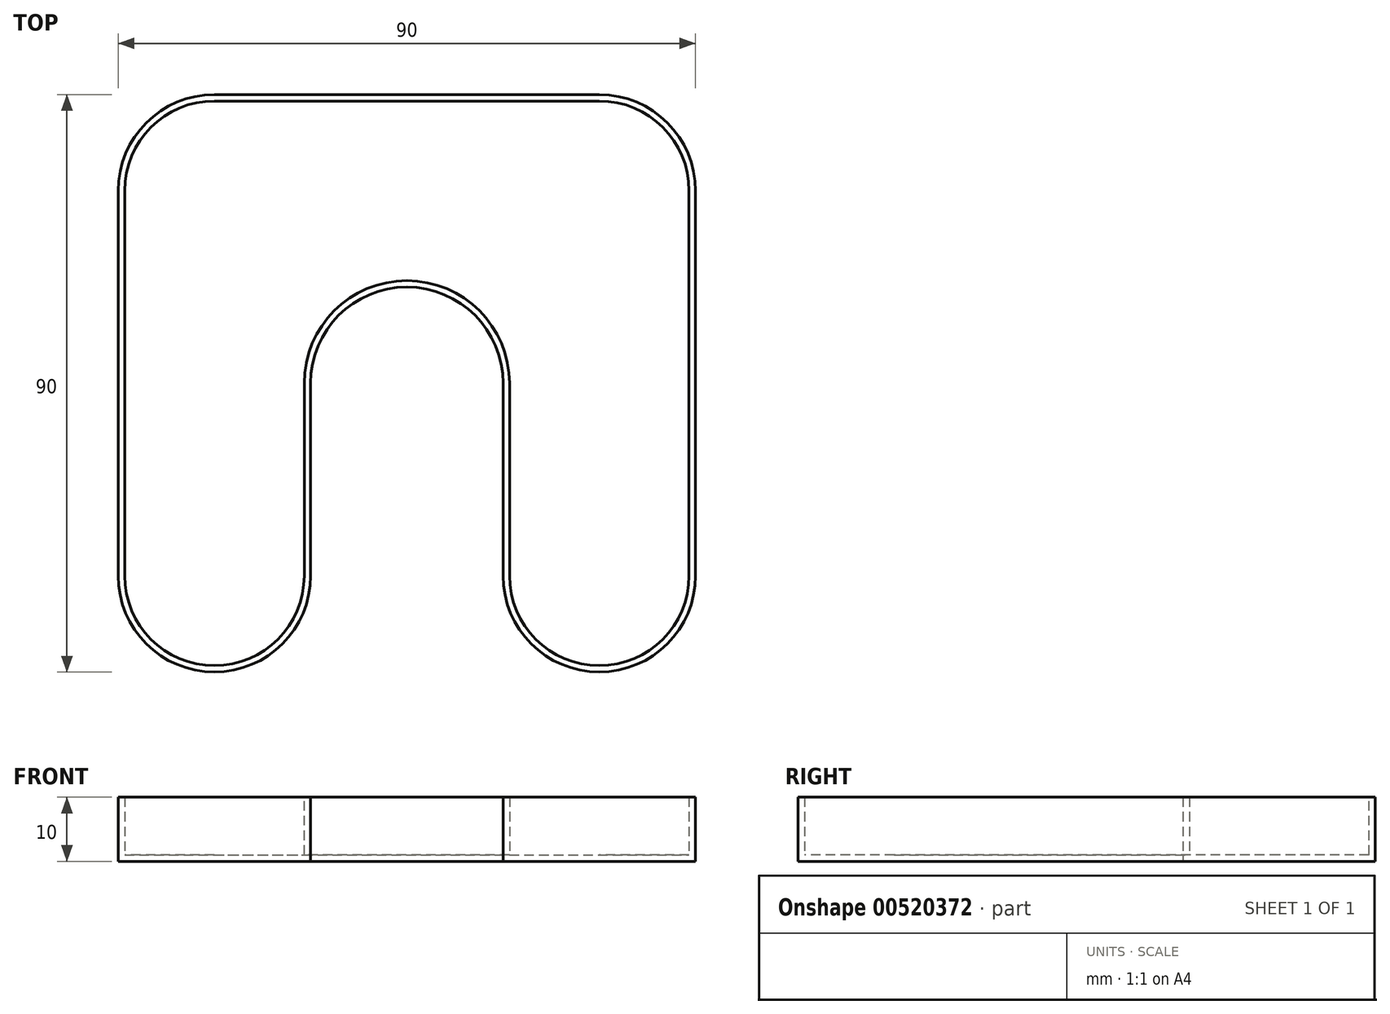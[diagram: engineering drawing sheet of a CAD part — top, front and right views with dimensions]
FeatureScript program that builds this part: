
annotation { "Feature Type Name" : "Feature", "Feature Type Description" : "" }
export const myFeature = defineFeature(function(context is Context, id is Id, definition is map)
    precondition{}
    {
        {
            var Q0;
            Q0=qCreatedBy(makeId("Top.planeOp"),FACE);
            var sketch = newSketch(context, id + "F0", { "sketchPlane" : qUnion([Q0])});
            skLineSegment(sketch, "E0.bottom", {"start": v(15, 73.88) * mm, "end": v(75, 73.88) * mm});
            skLineSegment(sketch, "E0.top", {"start": v(15, -16.12) * mm, "end": v(15, -16.12) * mm});
            skLineSegment(sketch, "E0.left", {"start": v(0, 58.88) * mm, "end": v(0, -1.12) * mm});
            skLineSegment(sketch, "E0.right", {"start": v(90, 58.88) * mm, "end": v(90, -1.12) * mm});
            skLineSegment(sketch, "E1", {"start": v(30, -1.12) * mm, "end": v(30, 28.88) * mm});
            skLineSegment(sketch, "E2", {"start": v(45, 43.88) * mm, "end": v(45, 43.88) * mm});
            skLineSegment(sketch, "E3", {"start": v(60, 28.88) * mm, "end": v(60, -1.12) * mm});
            skLineSegment(sketch, "E4.trimOffspring", {"start": v(75, -16.12) * mm, "end": v(75, -16.12) * mm});
            skPoint(sketch, "E5.visualSharp", {"position": v(0, 73.88) * mm});
            skArc(sketch, "E5.filletArc", {"start": v(15, 73.88) * mm, "mid": v(4.4, 69.48) * mm, "end": v(0, 58.88) * mm});
            skPoint(sketch, "E6.visualSharp", {"position": v(90, 73.88) * mm});
            skArc(sketch, "E6.filletArc", {"start": v(90, 58.88) * mm, "mid": v(85.6, 69.48) * mm, "end": v(75, 73.88) * mm});
            skPoint(sketch, "E7.visualSharp", {"position": v(90, -16.12) * mm});
            skArc(sketch, "E7.filletArc", {"start": v(75, -16.12) * mm, "mid": v(85.6, -11.73) * mm, "end": v(90, -1.12) * mm});
            skPoint(sketch, "E8.visualSharp", {"position": v(60, -16.12) * mm});
            skArc(sketch, "E8.filletArc", {"start": v(60, -1.12) * mm, "mid": v(64.4, -11.73) * mm, "end": v(75, -16.12) * mm});
            skPoint(sketch, "E9.visualSharp", {"position": v(30, -16.12) * mm});
            skArc(sketch, "E9.filletArc", {"start": v(15, -16.12) * mm, "mid": v(25.6, -11.73) * mm, "end": v(30, -1.12) * mm});
            skPoint(sketch, "E10.visualSharp", {"position": v(0, -16.12) * mm});
            skArc(sketch, "E10.filletArc", {"start": v(0, -1.12) * mm, "mid": v(4.4, -11.73) * mm, "end": v(15, -16.12) * mm});
            skPoint(sketch, "E11.visualSharp", {"position": v(30, 43.88) * mm});
            skArc(sketch, "E11.filletArc", {"start": v(45, 43.88) * mm, "mid": v(34.4, 39.48) * mm, "end": v(30, 28.88) * mm});
            skPoint(sketch, "E12.visualSharp", {"position": v(60, 43.88) * mm});
            skArc(sketch, "E12.filletArc", {"start": v(60, 28.88) * mm, "mid": v(55.6, 39.48) * mm, "end": v(45, 43.88) * mm});
            skSolve(sketch);
        }
        {
            var Q0;
            Q0 = qSketchRegion(id + "F0", true);
            extrude(context, id + "F1", {"entities" : qUnion([Q0]), "depth" : 10 * mm, "offsetDistance" : 25 * mm});
        }
        {
            var Q0;
            Q0=makeQuery(id+"F1.opExtrude","CAP_FACE",FACE,{"disambiguationData":[OSD([sQuery(id+"F0.wireOp",EDGE,"E0.bottom"),sQuery(id+"F0.wireOp",EDGE,"E0.left"),sQuery(id+"F0.wireOp",EDGE,"E0.right"),sQuery(id+"F0.wireOp",EDGE,"E1"),sQuery(id+"F0.wireOp",EDGE,"E3"),sQuery(id+"F0.wireOp",EDGE,"E5.filletArc"),sQuery(id+"F0.wireOp",EDGE,"E6.filletArc"),sQuery(id+"F0.wireOp",EDGE,"E7.filletArc"),sQuery(id+"F0.wireOp",EDGE,"E8.filletArc"),sQuery(id+"F0.wireOp",EDGE,"E9.filletArc"),sQuery(id+"F0.wireOp",EDGE,"E10.filletArc"),sQuery(id+"F0.wireOp",EDGE,"E11.filletArc"),sQuery(id+"F0.wireOp",EDGE,"E12.filletArc")])],"isStart":false});
            shell(context, id + "F2", {"entities" : qUnion([Q0]), "thickness" : 1 * mm});
        }
    });
